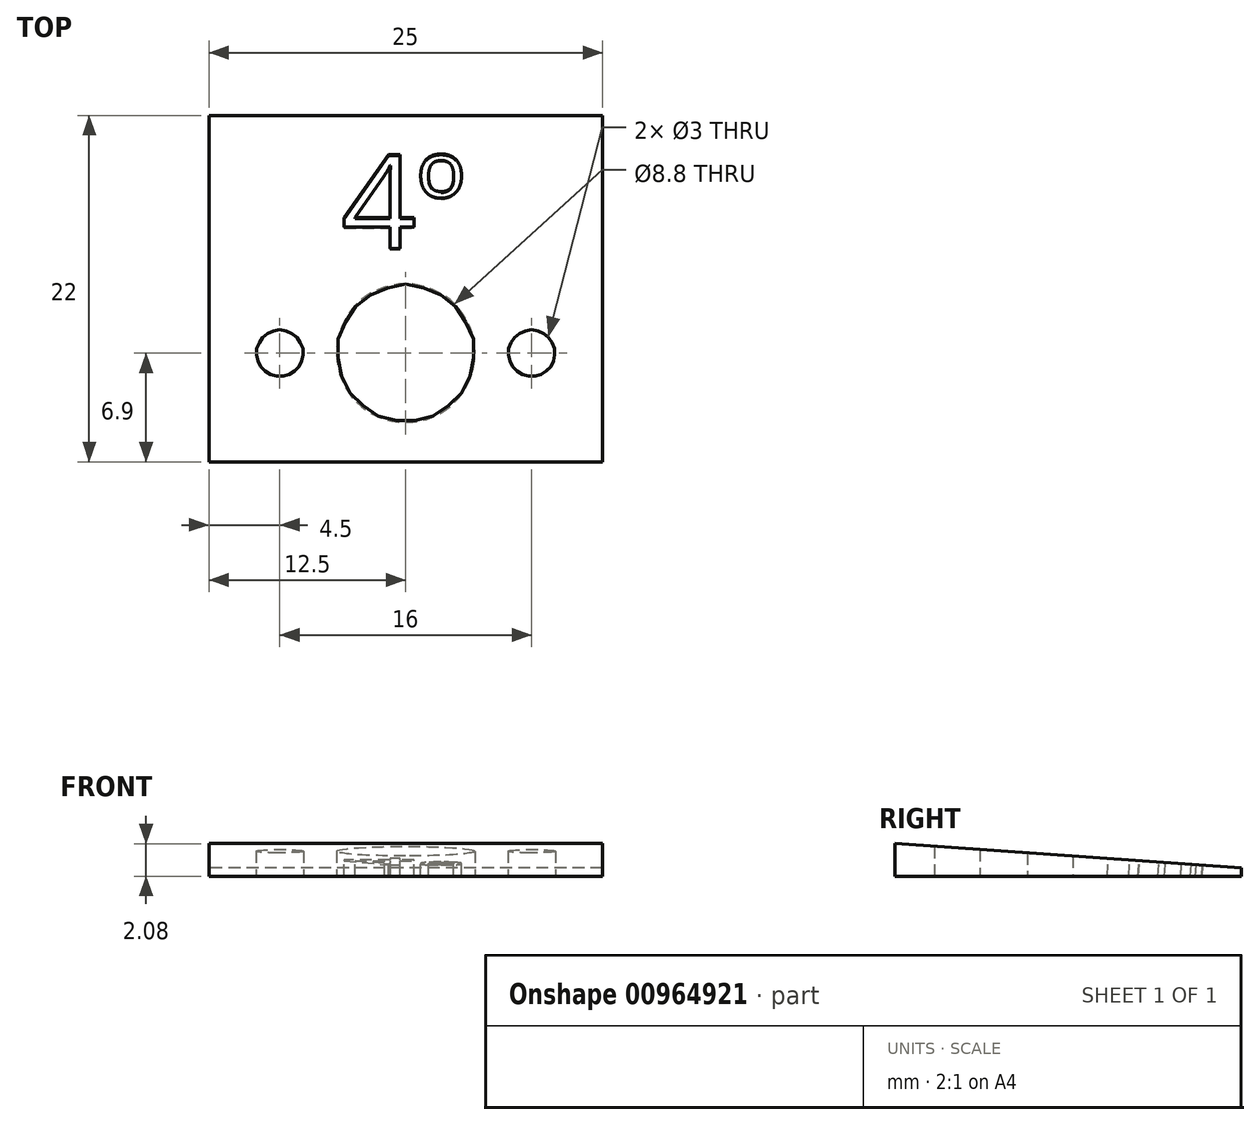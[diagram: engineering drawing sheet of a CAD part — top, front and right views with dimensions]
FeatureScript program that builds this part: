
annotation { "Feature Type Name" : "Feature", "Feature Type Description" : "" }
export const myFeature = defineFeature(function(context is Context, id is Id, definition is map)
    precondition{}
    {
        {
            var Q0;
            Q0=qCreatedBy(makeId("Right.planeOp"),FACE);
            var sketch = newSketch(context, id + "F0", { "sketchPlane" : qUnion([Q0])});
            skLineSegment(sketch, "E0", {"start": v(22, 0) * mm, "end": v(0, 0) * mm});
            skLineSegment(sketch, "E1", {"start": v(0, 0) * mm, "end": v(0, 2.08) * mm});
            skLineSegment(sketch, "E2", {"start": v(0, 2.08) * mm, "end": v(22, 0.54) * mm});
            skLineSegment(sketch, "E3", {"start": v(22, 0.54) * mm, "end": v(22, 0) * mm});
            skLineSegment(sketch, "E4", {"start": v(6.9, 1.6) * mm, "end": v(6.9, 0) * mm, "construction": true});
            skSolve(sketch);
        }
        {
            var Q0;
            Q0 = qSketchRegion(id + "F0", true);
            extrude(context, id + "F1", {"entities" : qUnion([Q0]), "endBound" : BoundingType.SYMMETRIC, "depth" : 25 * mm, "offsetDistance" : 25 * mm});
        }
        {
            var Q0;
            Q0=qCreatedBy(makeId("Top.planeOp"),FACE);
            var sketch = newSketch(context, id + "F2", { "sketchPlane" : qUnion([Q0])});
            skCircle(sketch, "E5", {"center": v(8, 6.9) * mm, "radius": 1.5 * mm});
            skCircle(sketch, "E6.MirrorC", {"center": v(-8, 6.9) * mm, "radius": 1.5 * mm});
            skCircle(sketch, "E7", {"center": v(0, 6.9) * mm, "radius": 4.4 * mm});
            skSolve(sketch);
        }
        {
            var Q0;
            Q0 = qSketchRegion(id + "F2", true);
            extrude(context, id + "F3", {"entities" : qUnion([Q0]), "operationType" : NewBodyOperationType.REMOVE, "depth" : 25 * mm, "offsetDistance" : 25 * mm});
        }
        {
            var Q0;
            Q0=makeQuery(id+"F1.opExtrude","SWEPT_FACE",FACE,{"disambiguationData":[OSD([sQuery(id+"F0.wireOp",EDGE,"E2")])]});
            var sketch = newSketch(context, id + "F4", { "sketchPlane" : qUnion([Q0])});
            skText(sketch, "E8", { "text": "4º", "fontName": "OpenSans-Regular.ttf"});
            const initialGuessF4  = {"E8": [-0.00408, 0.01344, 1, 0, 0.006]};
            skSetInitialGuess(sketch, initialGuessF4);
            skSolve(sketch);
        }
        {
            var Q0;
            Q0 = qSketchRegion(id + "F4", true);
            extrude(context, id + "F5", {"entities" : qUnion([Q0]), "operationType" : NewBodyOperationType.REMOVE, "oppositeDirection" : true, "depth" : 25 * mm, "offsetDistance" : 25 * mm});
        }
    });
